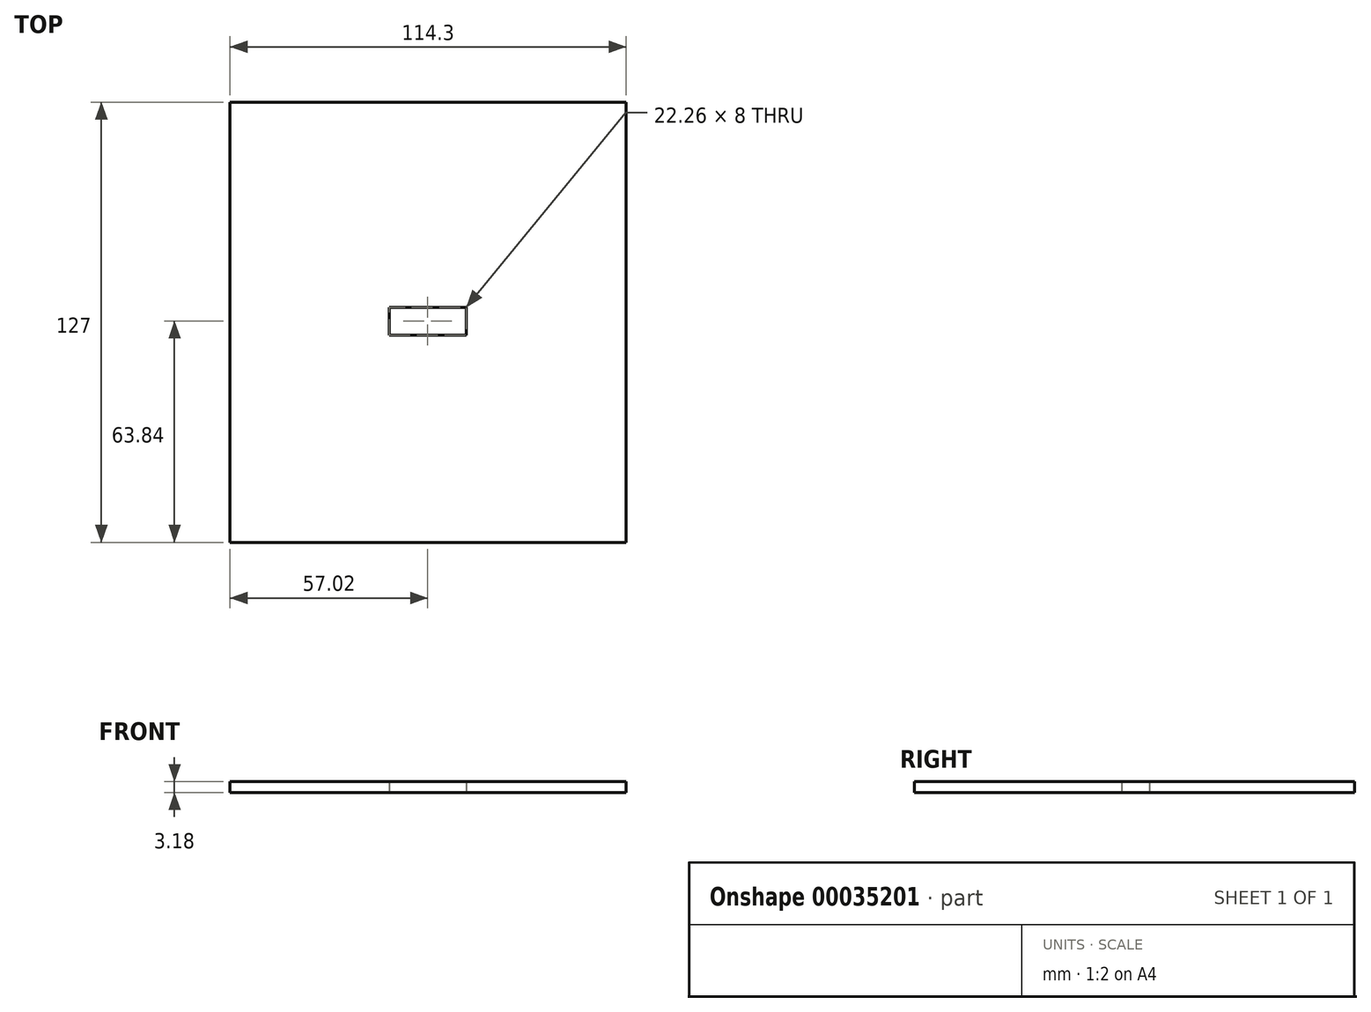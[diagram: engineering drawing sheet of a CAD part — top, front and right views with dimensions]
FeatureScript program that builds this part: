
annotation { "Feature Type Name" : "Feature", "Feature Type Description" : "" }
export const myFeature = defineFeature(function(context is Context, id is Id, definition is map)
    precondition{}
    {
        {
            var Q0;
            Q0=qCreatedBy(makeId("Top.planeOp"),FACE);
            var sketch = newSketch(context, id + "F0", { "sketchPlane" : qUnion([Q0])});
            skLineSegment(sketch, "E0.bottom", {"start": v(-57.02, 63.16) * mm, "end": v(57.28, 63.16) * mm});
            skLineSegment(sketch, "E0.top", {"start": v(-57.02, -63.84) * mm, "end": v(57.28, -63.84) * mm});
            skLineSegment(sketch, "E0.left", {"start": v(-57.02, 63.16) * mm, "end": v(-57.02, -63.84) * mm});
            skLineSegment(sketch, "E0.right", {"start": v(57.28, 63.16) * mm, "end": v(57.28, -63.84) * mm});
            skLineSegment(sketch, "E1.rect.bottom", {"start": v(-11.13, 4) * mm, "end": v(11.13, 4) * mm});
            skLineSegment(sketch, "E1.rect.top", {"start": v(-11.13, -4) * mm, "end": v(11.13, -4) * mm});
            skLineSegment(sketch, "E1.rect.left", {"start": v(-11.13, 4) * mm, "end": v(-11.13, -4) * mm});
            skLineSegment(sketch, "E1.rect.right", {"start": v(11.13, 4) * mm, "end": v(11.13, -4) * mm});
            skPoint(sketch, "E1.rect.middle", {"position": v(0, 0) * mm});
            skSolve(sketch);
        }
        {
            var Q0;
            Q0=makeQuery(id+"F0.imprint","IMPRINT",FACE,{"disambiguationData":[TD([[makeQuery(id+"F0.imprint","IMPRINT",EDGE,{"derivedFrom":sQuery(id+"F0.wireOp",EDGE,"E0.bottom")}),-1.0]])]});
            extrude(context, id + "F1", {"entities" : qUnion([Q0]), "depth" : 3.18 * mm});
        }
    });
